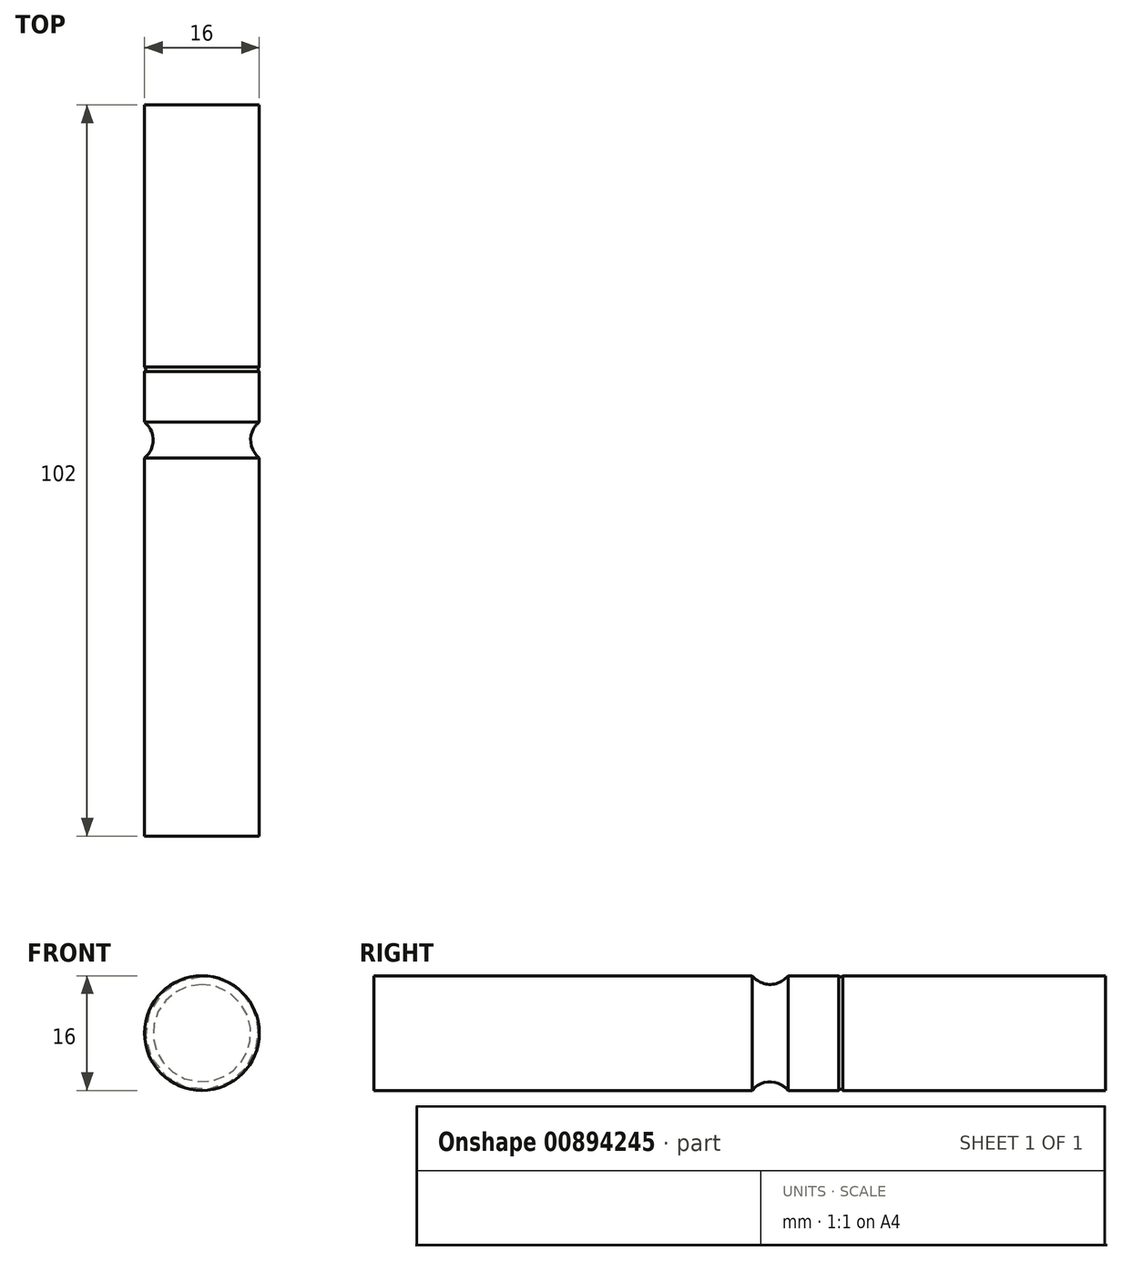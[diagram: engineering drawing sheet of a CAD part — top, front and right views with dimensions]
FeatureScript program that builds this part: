
annotation { "Feature Type Name" : "Feature", "Feature Type Description" : "" }
export const myFeature = defineFeature(function(context is Context, id is Id, definition is map)
    precondition{}
    {
        {
            var Q0;
            Q0=qCreatedBy(makeId("Right.planeOp"),FACE);
            var sketch = newSketch(context, id + "F0", { "sketchPlane" : qUnion([Q0])});
            skLineSegment(sketch, "E0", {"start": v(0, 0) * mm, "end": v(0, 8) * mm});
            skLineSegment(sketch, "E1", {"start": v(0, 8) * mm, "end": v(52.75, 8) * mm});
            skArc(sketch, "E2", {"start": v(52.75, 8) * mm, "mid": v(55.25, 6.8) * mm, "end": v(57.75, 8) * mm});
            skLineSegment(sketch, "E3", {"start": v(57.75, 8) * mm, "end": v(64.79, 8) * mm});
            skArc(sketch, "E4", {"start": v(64.79, 8) * mm, "mid": v(65.1, 7.85) * mm, "end": v(65.41, 8) * mm});
            skLineSegment(sketch, "E5", {"start": v(65.41, 8) * mm, "end": v(102, 8) * mm});
            skLineSegment(sketch, "E6", {"start": v(102, 8) * mm, "end": v(102, 0) * mm});
            skLineSegment(sketch, "E7", {"start": v(102, 0) * mm, "end": v(0, 0) * mm});
            skSolve(sketch);
        }
        {
            var Q0;
            Q0=makeQuery(id+"F0.imprint","IMPRINT",FACE,{"disambiguationData":[TD([[makeQuery(id+"F0.imprint","IMPRINT",EDGE,{"derivedFrom":sQuery(id+"F0.wireOp",EDGE,"E0")}),-1.0]])]});
            var Q1;
            Q1=sQuery(id+"F0.wireOp",EDGE,"E7");
            revolve(context, id + "F1", {"surfaceOperationType" : NewSurfaceOperationType.NEW, "entities" : qUnion([Q0]), "axis" : qUnion([Q1]), "revolveType" : RevolveType.FULL});
        }
    });
